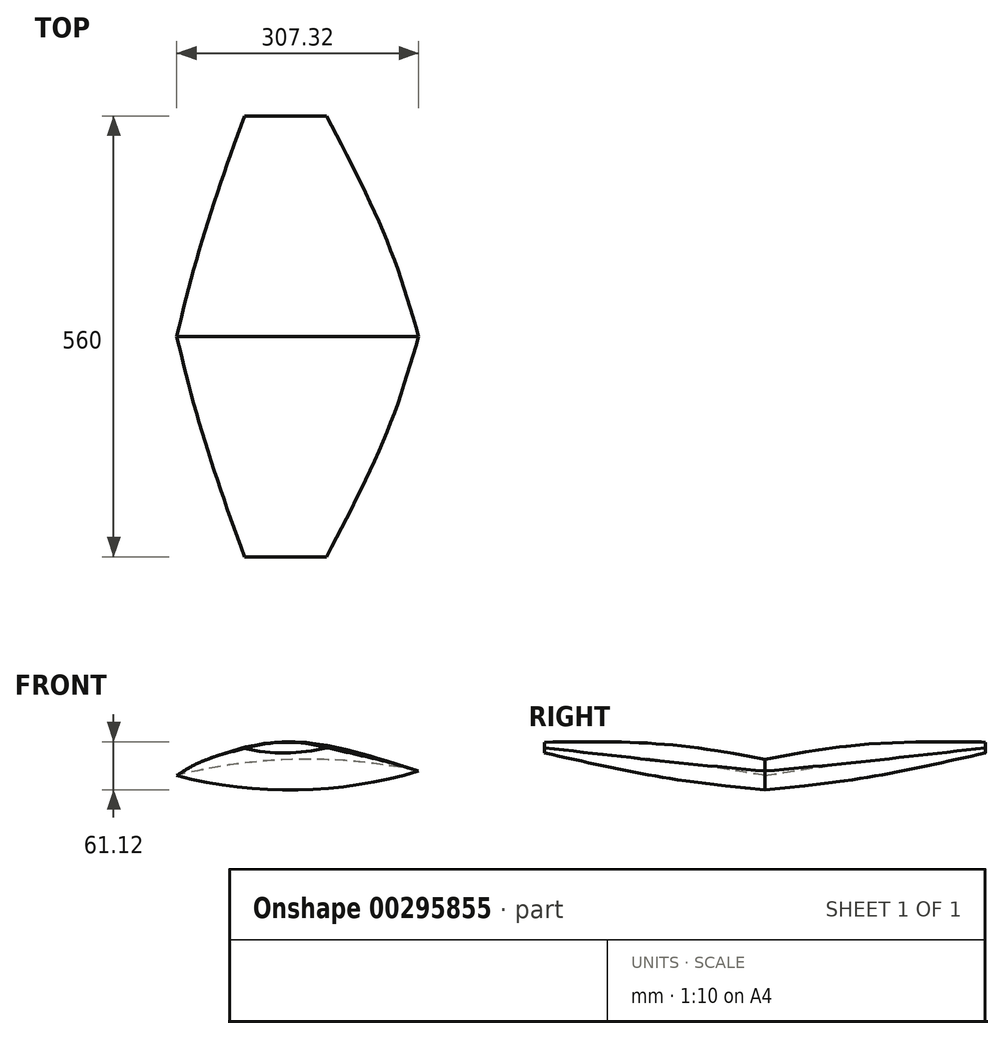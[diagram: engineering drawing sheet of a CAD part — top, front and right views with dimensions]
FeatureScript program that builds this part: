
annotation { "Feature Type Name" : "Feature", "Feature Type Description" : "" }
export const myFeature = defineFeature(function(context is Context, id is Id, definition is map)
    precondition{}
    {
        {
            var Q0;
            Q0=qCreatedBy(makeId("Front.planeOp"),FACE);
            cPlane(context, id + "F0", {"entities" : qUnion([Q0]), "cplaneType" : CPlaneType.OFFSET, "offset" : 103 * mm, "oppositeDirection" : true, "width" : 150 * mm, "height" : 150 * mm});
        }
        {
            var Q0;
            Q0=qCreatedBy(makeId("Front.planeOp"),FACE);
            cPlane(context, id + "F1", {"entities" : qUnion([Q0]), "cplaneType" : CPlaneType.OFFSET, "offset" : 177 * mm, "width" : 150 * mm, "height" : 150 * mm});
        }
        {
            var Q0;
            Q0=qCreatedBy(makeId("Front.planeOp"),FACE);
            var sketch = newSketch(context, id + "F2", { "sketchPlane" : qUnion([Q0])});
            skArc(sketch, "E0", {"start": v(139.55, 0) * mm, "mid": v(15.76, 21.76) * mm, "end": v(-108.03, 0) * mm});
            skArc(sketch, "E1", {"start": v(-108.03, 0) * mm, "mid": v(15.76, -22.13) * mm, "end": v(139.55, 0) * mm});
            skSolve(sketch);
        }
        {
            var Q0;
            Q0=qCreatedBy(id+"F0.planeOp",FACE);
            var sketch = newSketch(context, id + "F3", { "sketchPlane" : qUnion([Q0])});
            skArc(sketch, "E2", {"start": v(178.98, -11.31) * mm, "mid": v(21.89, 5.06) * mm, "end": v(-134.7, -15.6) * mm});
            skArc(sketch, "E3", {"start": v(-134.7, -15.6) * mm, "mid": v(19.35, -33.69) * mm, "end": v(172.62, -9.92) * mm});
            skSolve(sketch);
        }
        {
            var Q0;
            Q0=qCreatedBy(id+"F1.planeOp",FACE);
            var sketch = newSketch(context, id + "F4", { "sketchPlane" : qUnion([Q0])});
            skArc(sketch, "E4", {"start": v(-48.77, 18.85) * mm, "mid": v(3.58, 13.24) * mm, "end": v(55.83, 19.79) * mm});
            skArc(sketch, "E5", {"start": v(55.83, 19.79) * mm, "mid": v(3.46, 26.8) * mm, "end": v(-48.77, 18.85) * mm});
            skSolve(sketch);
        }
        {
            var Q0;
            {var subQ0=sQuery(id+"F3.wireOp",EDGE,"E3");Q0=makeQuery(id+"F3.imprint","IMPRINT",FACE,{"disambiguationData":[TD([[makeQuery(id+"F3.imprint","IMPRINT",EDGE,{"derivedFrom":subQ0}),1.0]])]});}
            var Q1;
            Q1=makeQuery(id+"F2.imprint","IMPRINT",FACE,{"disambiguationData":[TD([[makeQuery(id+"F2.imprint","IMPRINT",EDGE,{"derivedFrom":sQuery(id+"F2.wireOp",EDGE,"E0")}),1.0]])]});
            var Q2;
            Q2=makeQuery(id+"F4.imprint","IMPRINT",FACE,{"disambiguationData":[TD([[makeQuery(id+"F4.imprint","IMPRINT",EDGE,{"derivedFrom":sQuery(id+"F4.wireOp",EDGE,"E4")}),1.0]])]});
            loft(context, id + "F5", {"bodyType" : ToolBodyType.SURFACE, "wireProfilesArray" : [{ "wireProfileEntities" : qUnion([Q0]) }, { "wireProfileEntities" : qUnion([Q1]) }, { "wireProfileEntities" : qUnion([Q2]) }]});
        }
        {
            var Q0;
            Q0=makeQuery(id+"F5.opLoft","SWEPT_BODY",BODY,{"disambiguationData":[OSD([sQuery(id+"F2.wireOp",EDGE,"E0"),sQuery(id+"F3.wireOp",EDGE,"E2"),sQuery(id+"F4.wireOp",EDGE,"E4")])]});
            var Q1;
            Q1=qCreatedBy(id+"F0.planeOp",FACE);
            mirror(context, id + "F6", {"entities" : qUnion([Q0]), "mirrorPlane" : qUnion([Q1])});
        }
    });
